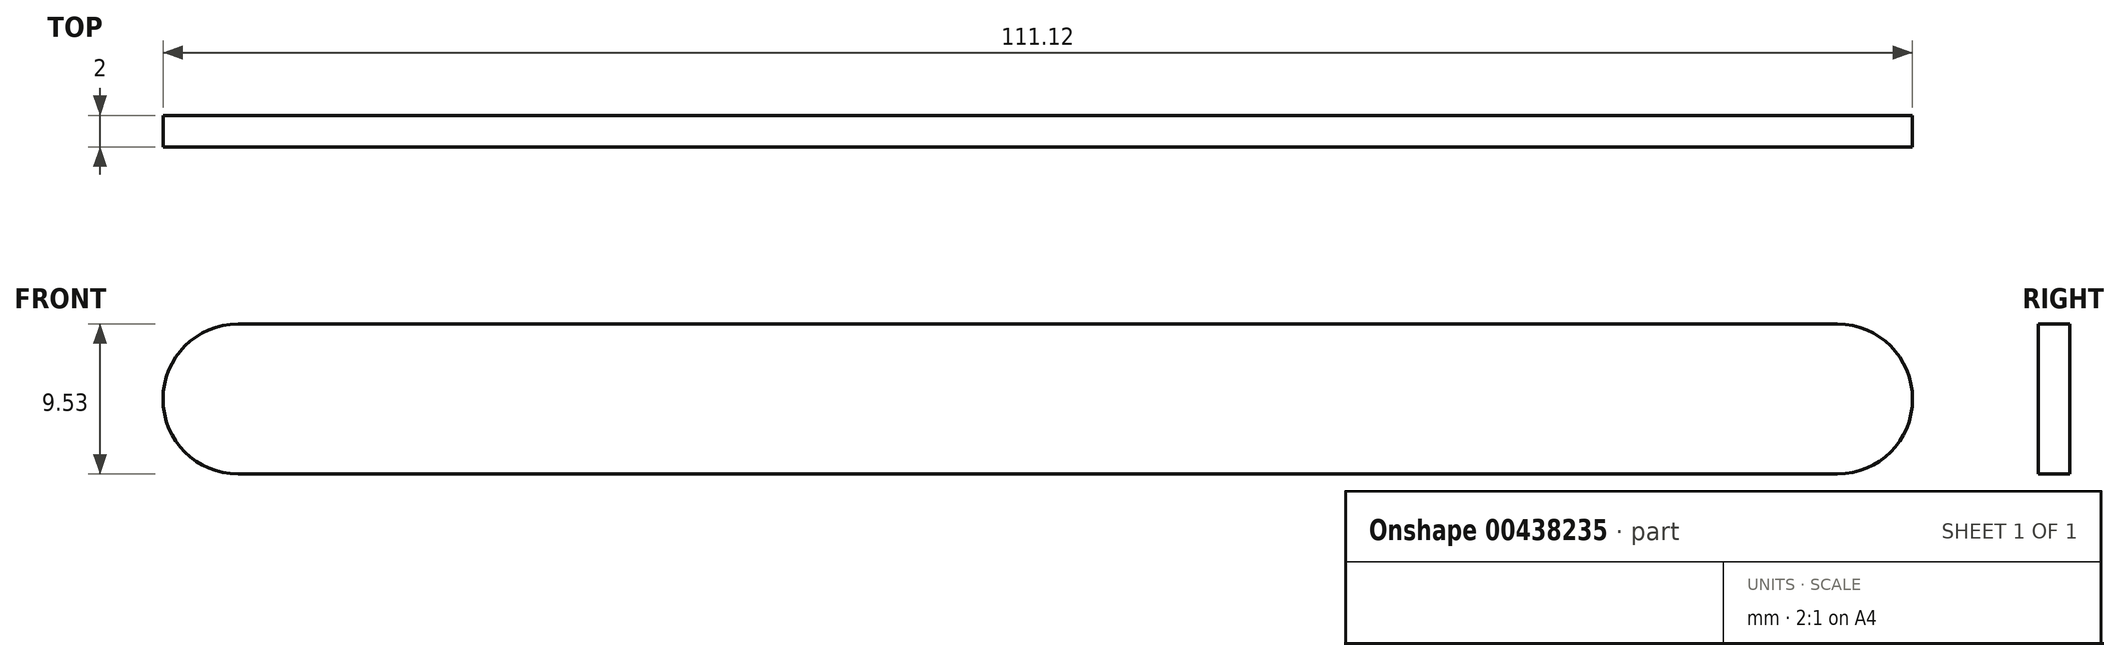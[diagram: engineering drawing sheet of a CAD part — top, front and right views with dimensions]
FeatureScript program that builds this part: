
annotation { "Feature Type Name" : "Feature", "Feature Type Description" : "" }
export const myFeature = defineFeature(function(context is Context, id is Id, definition is map)
    precondition{}
    {
        {
            var Q0;
            Q0=qCreatedBy(makeId("Front.planeOp"),FACE);
            var sketch = newSketch(context, id + "F0", { "sketchPlane" : qUnion([Q0])});
            skLineSegment(sketch, "E0", {"start": v(-64.22, 10.78) * mm, "end": v(-64.22, 1.25) * mm});
            skLineSegment(sketch, "E1", {"start": v(-64.22, 1.25) * mm, "end": v(37.38, 1.25) * mm});
            skLineSegment(sketch, "E2", {"start": v(37.38, 1.25) * mm, "end": v(37.38, 10.78) * mm});
            skLineSegment(sketch, "E3", {"start": v(37.38, 10.78) * mm, "end": v(-64.22, 10.78) * mm});
            skArc(sketch, "E4", {"start": v(-64.22, 10.78) * mm, "mid": v(-68.98, 6.02) * mm, "end": v(-64.22, 1.25) * mm});
            skArc(sketch, "E5", {"start": v(37.38, 1.25) * mm, "mid": v(42.14, 6.02) * mm, "end": v(37.38, 10.78) * mm});
            skSolve(sketch);
        }
        {
            var Q0;
            Q0 = qSketchRegion(id + "F0", true);
            extrude(context, id + "F1", {"entities" : qUnion([Q0]), "depth" : 2 * mm});
        }
    });
